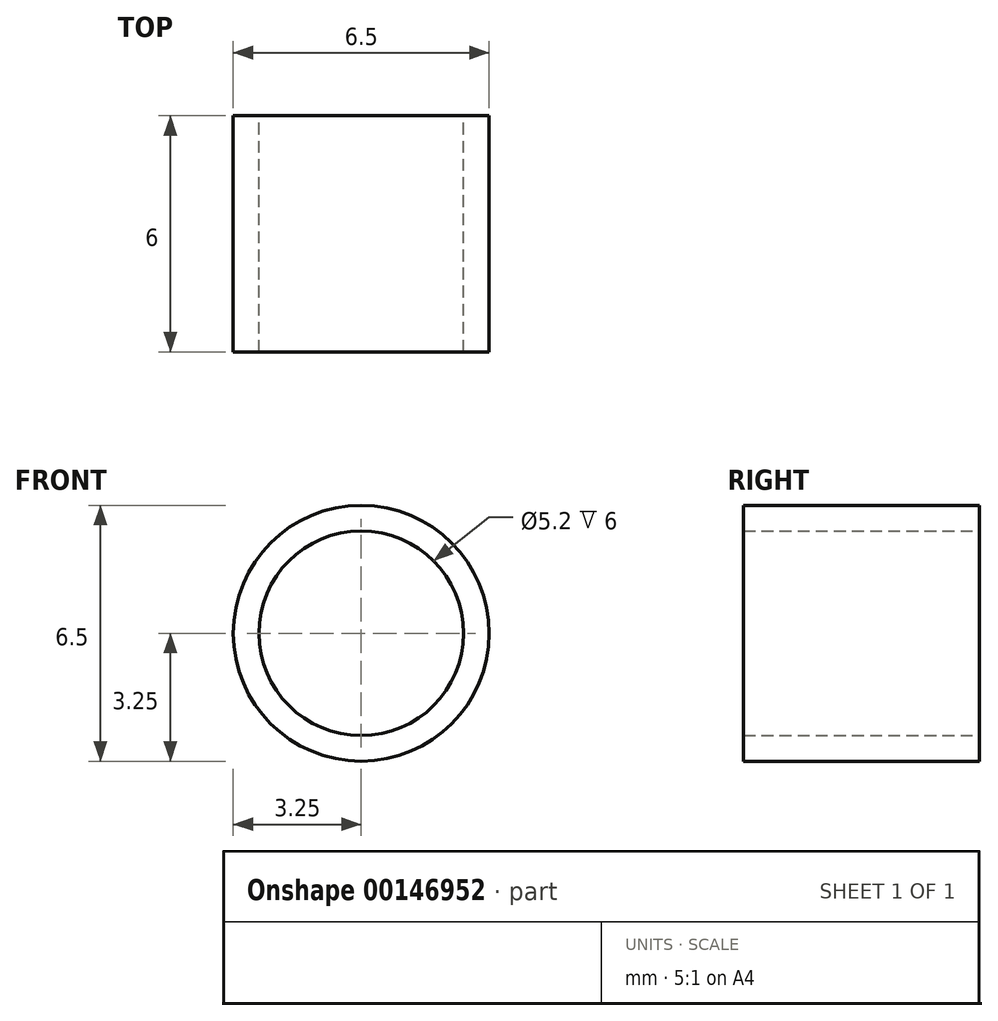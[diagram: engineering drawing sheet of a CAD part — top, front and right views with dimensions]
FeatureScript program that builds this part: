
annotation { "Feature Type Name" : "Feature", "Feature Type Description" : "" }
export const myFeature = defineFeature(function(context is Context, id is Id, definition is map)
    precondition{}
    {
        {
            var Q0;
            Q0=qCreatedBy(makeId("Front.planeOp"),FACE);
            var sketch = newSketch(context, id + "F0", { "sketchPlane" : qUnion([Q0])});
            skCircle(sketch, "E0", {"center": v(0, 0) * mm, "radius": 2.6 * mm});
            skCircle(sketch, "E1", {"center": v(0, 0) * mm, "radius": 3.25 * mm});
            skSolve(sketch);
        }
        {
            var Q0;
            Q0 = qSketchRegion(id + "F0", true);
            extrude(context, id + "F1", {"entities" : qUnion([Q0]), "depth" : 6 * mm});
        }
    });
